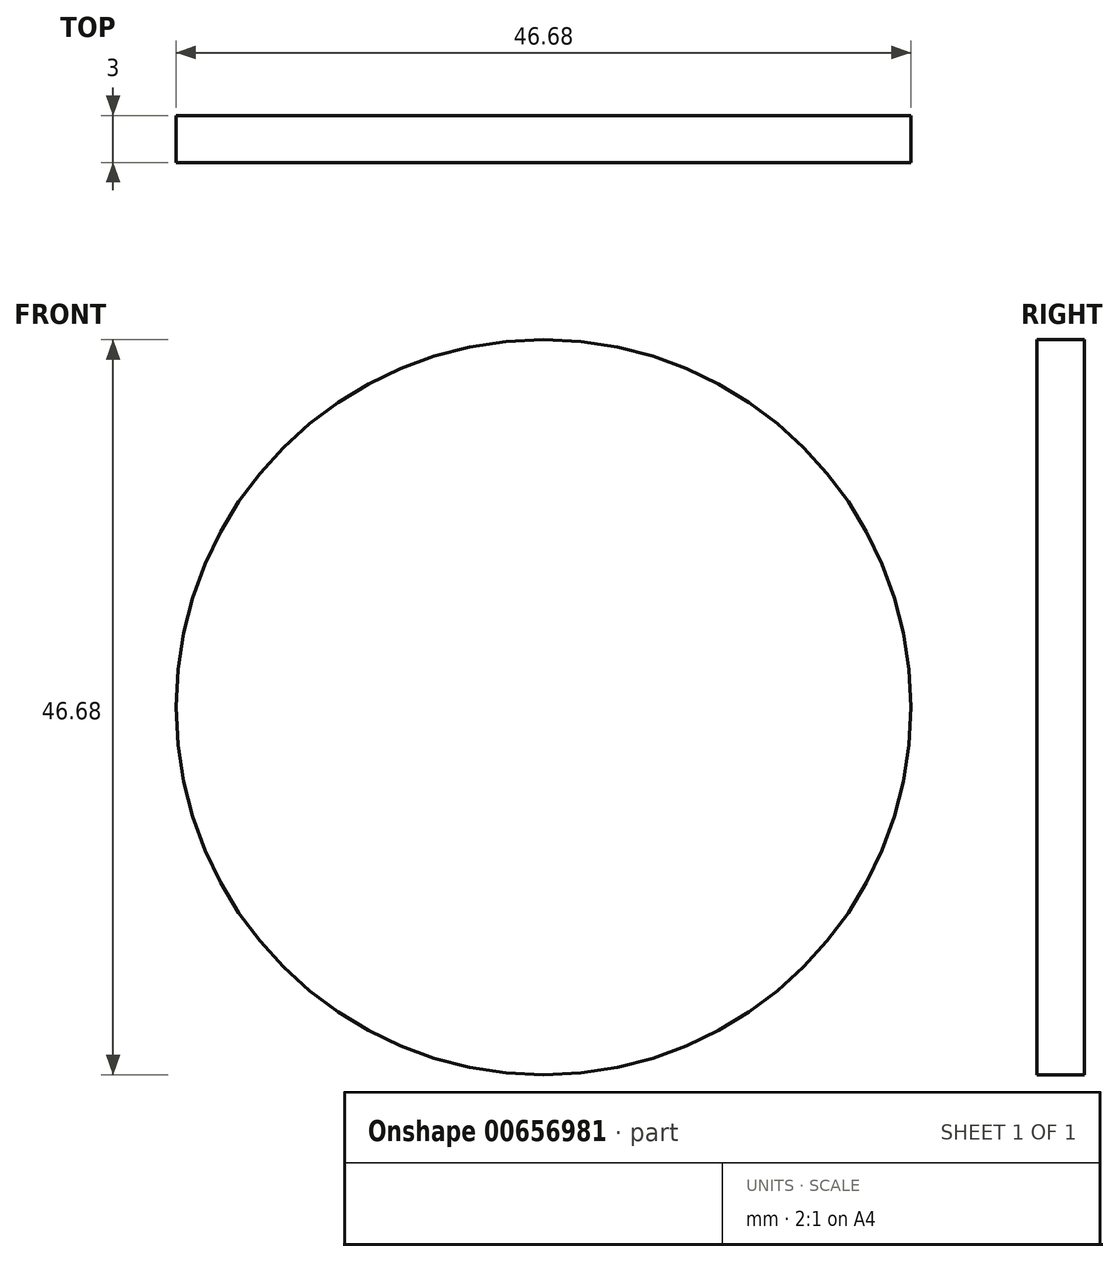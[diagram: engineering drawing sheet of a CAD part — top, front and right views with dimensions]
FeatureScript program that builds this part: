
annotation { "Feature Type Name" : "Feature", "Feature Type Description" : "" }
export const myFeature = defineFeature(function(context is Context, id is Id, definition is map)
    precondition{}
    {
        {
            var Q0;
            Q0=qCreatedBy(makeId("Front.planeOp"),FACE);
            var sketch = newSketch(context, id + "F0", { "sketchPlane" : qUnion([Q0])});
            skCircle(sketch, "E0", {"center": v(0, 0) * mm, "radius": 23.34 * mm});
            skSolve(sketch);
        }
        {
            var Q0;
            Q0=makeQuery(id+"F0.imprint","IMPRINT",FACE,{"disambiguationData":[TD([[makeQuery(id+"F0.imprint","IMPRINT",EDGE,{"derivedFrom":sQuery(id+"F0.wireOp",EDGE,"E0")}),1.0]])]});
            extrude(context, id + "F1", {"entities" : qUnion([Q0]), "depth" : 3 * mm, "offsetDistance" : 25 * mm});
        }
    });
